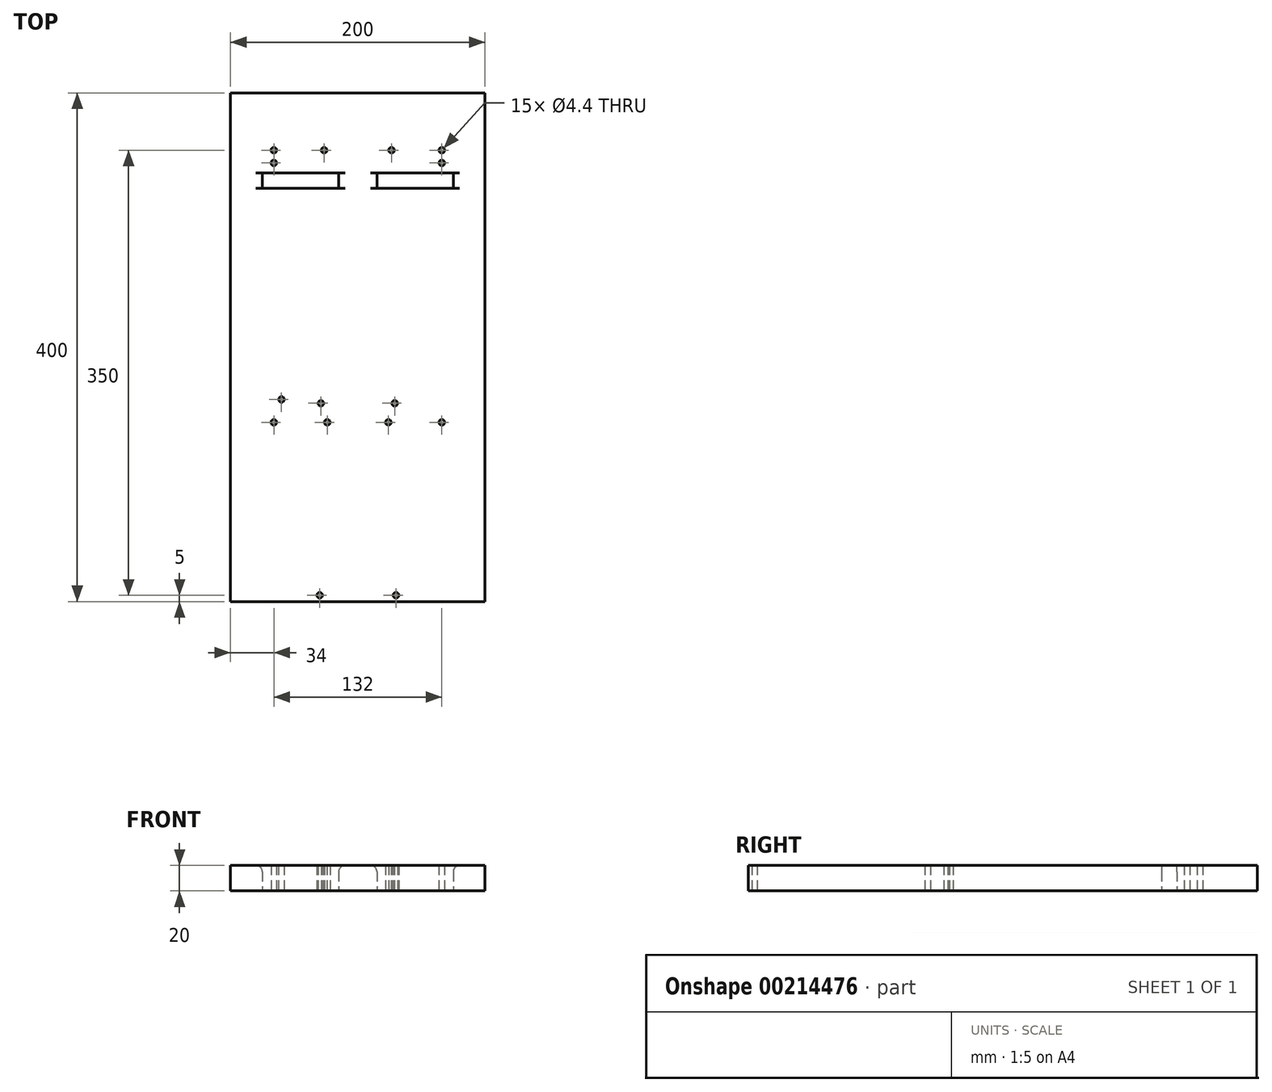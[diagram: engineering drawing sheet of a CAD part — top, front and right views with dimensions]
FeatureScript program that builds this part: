
annotation { "Feature Type Name" : "Feature", "Feature Type Description" : "" }
export const myFeature = defineFeature(function(context is Context, id is Id, definition is map)
    precondition{}
    {
        {
            var Q0;
            Q0=qCreatedBy(makeId("Top.planeOp"),FACE);
            var sketch = newSketch(context, id + "F0", { "sketchPlane" : qUnion([Q0])});
            skLineSegment(sketch, "E0.bottom", {"start": v(100, 200) * mm, "end": v(-100, 200) * mm});
            skLineSegment(sketch, "E0.top", {"start": v(100, -200) * mm, "end": v(-100, -200) * mm});
            skLineSegment(sketch, "E0.left", {"start": v(100, 200) * mm, "end": v(100, -200) * mm});
            skLineSegment(sketch, "E0.right", {"start": v(-100, 200) * mm, "end": v(-100, -200) * mm});
            skPoint(sketch, "E0.middle", {"position": v(0, 0) * mm});
            skLineSegment(sketch, "E1", {"start": v(100, 155) * mm, "end": v(-100, 155) * mm, "construction": true});
            skLineSegment(sketch, "E2", {"start": v(0, 200) * mm, "end": v(0, -200) * mm, "construction": true});
            skPoint(sketch, "E3", {"position": v(-26.5, 155) * mm});
            skPoint(sketch, "E4", {"position": v(26.5, 155) * mm});
            skLineSegment(sketch, "E5", {"start": v(-45, 200) * mm, "end": v(-45, -200) * mm, "construction": true});
            skLineSegment(sketch, "E6", {"start": v(-100, -59) * mm, "end": v(100, -59) * mm, "construction": true});
            skPoint(sketch, "E7", {"position": v(-66, -59) * mm});
            skPoint(sketch, "E8.MirrorP", {"position": v(-24, -59) * mm});
            skPoint(sketch, "E9.MirrorP", {"position": v(66, -59) * mm});
            skPoint(sketch, "E10.MirrorP", {"position": v(24, -59) * mm});
            skLineSegment(sketch, "E11", {"start": v(-66, 200) * mm, "end": v(-66, 89.73) * mm, "construction": true});
            skPoint(sketch, "E12", {"position": v(-66, 155) * mm});
            skPoint(sketch, "E13", {"position": v(-66, 145) * mm});
            skPoint(sketch, "E14.MirrorP", {"position": v(66, 155) * mm});
            skPoint(sketch, "E15.MirrorP", {"position": v(66, 145) * mm});
            skLineSegment(sketch, "E16.bottom", {"start": v(-75, 125) * mm, "end": v(-15, 125) * mm});
            skLineSegment(sketch, "E16.top", {"start": v(-75, 137) * mm, "end": v(-15, 137) * mm});
            skLineSegment(sketch, "E16.left", {"start": v(-75, 125) * mm, "end": v(-75, 137) * mm});
            skLineSegment(sketch, "E16.right", {"start": v(-15, 125) * mm, "end": v(-15, 137) * mm});
            skPoint(sketch, "E16.middle", {"position": v(-45, 131) * mm});
            skLineSegment(sketch, "E17.MirrorCS", {"start": v(15, 125) * mm, "end": v(15, 137) * mm});
            skLineSegment(sketch, "E18.MirrorCS", {"start": v(75, 137) * mm, "end": v(15, 137) * mm});
            skLineSegment(sketch, "E19.MirrorCS", {"start": v(75, 125) * mm, "end": v(15, 125) * mm});
            skLineSegment(sketch, "E20.MirrorCS", {"start": v(75, 125) * mm, "end": v(75, 137) * mm});
            skLineSegment(sketch, "E21", {"start": v(-100, -195) * mm, "end": v(100, -195) * mm, "construction": true});
            skLineSegment(sketch, "E22", {"start": v(100, -44) * mm, "end": v(-100, -44) * mm, "construction": true});
            skPoint(sketch, "E23", {"position": v(-30, -195) * mm});
            skPoint(sketch, "E24", {"position": v(-29, -44) * mm});
            skPoint(sketch, "E25.MirrorP", {"position": v(29, -44) * mm});
            skPoint(sketch, "E26.MirrorP", {"position": v(30, -195) * mm});
            skPoint(sketch, "E27", {"position": v(-60, -41) * mm});
            skSolve(sketch);
        }
        {
            var Q0;
            Q0=makeQuery(id+"F0.imprint","IMPRINT",FACE,{"disambiguationData":[TD([[makeQuery(id+"F0.imprint","IMPRINT",EDGE,{"derivedFrom":sQuery(id+"F0.wireOp",EDGE,"E0.bottom")}),1.0]])]});
            extrude(context, id + "F1", {"entities" : qUnion([Q0]), "depth" : 20 * mm});
        }
        {
            var Q0;
            Q0=sQuery(id+"F0.wireOp",VERTEX,"E3");
            var Q1;
            Q1=sQuery(id+"F0.wireOp",VERTEX,"E4");
            var Q2;
            Q2=sQuery(id+"F0.wireOp",VERTEX,"E7");
            var Q3;
            Q3=sQuery(id+"F0.wireOp",VERTEX,"E8.MirrorP");
            var Q4;
            Q4=sQuery(id+"F0.wireOp",VERTEX,"E10.MirrorP");
            var Q5;
            Q5=sQuery(id+"F0.wireOp",VERTEX,"E9.MirrorP");
            var Q6;
            Q6=sQuery(id+"F0.wireOp",VERTEX,"E12");
            var Q7;
            Q7=sQuery(id+"F0.wireOp",VERTEX,"E13");
            var Q8;
            Q8=sQuery(id+"F0.wireOp",VERTEX,"E14.MirrorP");
            var Q9;
            Q9=sQuery(id+"F0.wireOp",VERTEX,"E15.MirrorP");
            var Q10;
            Q10=sQuery(id+"F0.wireOp",VERTEX,"E24");
            var Q11;
            Q11=sQuery(id+"F0.wireOp",VERTEX,"E25.MirrorP");
            var Q12;
            Q12=sQuery(id+"F0.wireOp",VERTEX,"E23");
            var Q13;
            Q13=sQuery(id+"F0.wireOp",VERTEX,"E26.MirrorP");
            var Q14;
            Q14=sQuery(id+"F0.wireOp",VERTEX,"E27");
            var Q15;
            Q15=makeQuery(id+"F1.opExtrude","SWEPT_BODY",BODY,{"disambiguationData":[OSD([sQuery(id+"F0.wireOp",EDGE,"E0.bottom"),sQuery(id+"F0.wireOp",EDGE,"E0.top"),sQuery(id+"F0.wireOp",EDGE,"E0.left"),sQuery(id+"F0.wireOp",EDGE,"E0.right")])]});
            hole(context, id + "F2", {"style" : HoleStyle.SIMPLE, "endStyle" : HoleEndStyle.THROUGH, "oppositeDirection" : true, "standardTappedOrClearance" : lookupTablePath({ "standard" : "ISO", "fit" : "Normal", "size" : "M4", "type" : "Clearance" }), "standardBlindInLast" : lookupTablePath({ "fit" : "Standard", "standard" : "ISO", "size" : "M4", "type" : "Clearance" }), "holeDiameter" : 4.4 * mm, "locations" : qUnion([Q0, Q1, Q2, Q3, Q4, Q5, Q6, Q7, Q8, Q9, Q10, Q11, Q12, Q13, Q14]), "scope" : qUnion([Q15]), "isTappedThrough" : true});
        }
        {
            var Q0;
            Q0=makeQuery(id+"F1.opExtrude","CAP_EDGE",EDGE,{"disambiguationData":[OSD([sQuery(id+"F0.wireOp",EDGE,"E16.left")])],"isStart":false});
            var Q1;
            Q1=makeQuery(id+"F1.opExtrude","CAP_EDGE",EDGE,{"disambiguationData":[OSD([sQuery(id+"F0.wireOp",EDGE,"E16.right")])],"isStart":false});
            var Q2;
            Q2=makeQuery(id+"F1.opExtrude","CAP_EDGE",EDGE,{"disambiguationData":[OSD([sQuery(id+"F0.wireOp",EDGE,"E17.MirrorCS")])],"isStart":false});
            var Q3;
            Q3=makeQuery(id+"F1.opExtrude","CAP_EDGE",EDGE,{"disambiguationData":[OSD([sQuery(id+"F0.wireOp",EDGE,"E20.MirrorCS")])],"isStart":false});
            fillet(context, id + "F3", {"entities" : qUnion([Q0, Q1, Q2, Q3]), "radius" : 5 * mm, "tangentPropagation" : true, "allowEdgeOverflow" : false});
        }
    });
